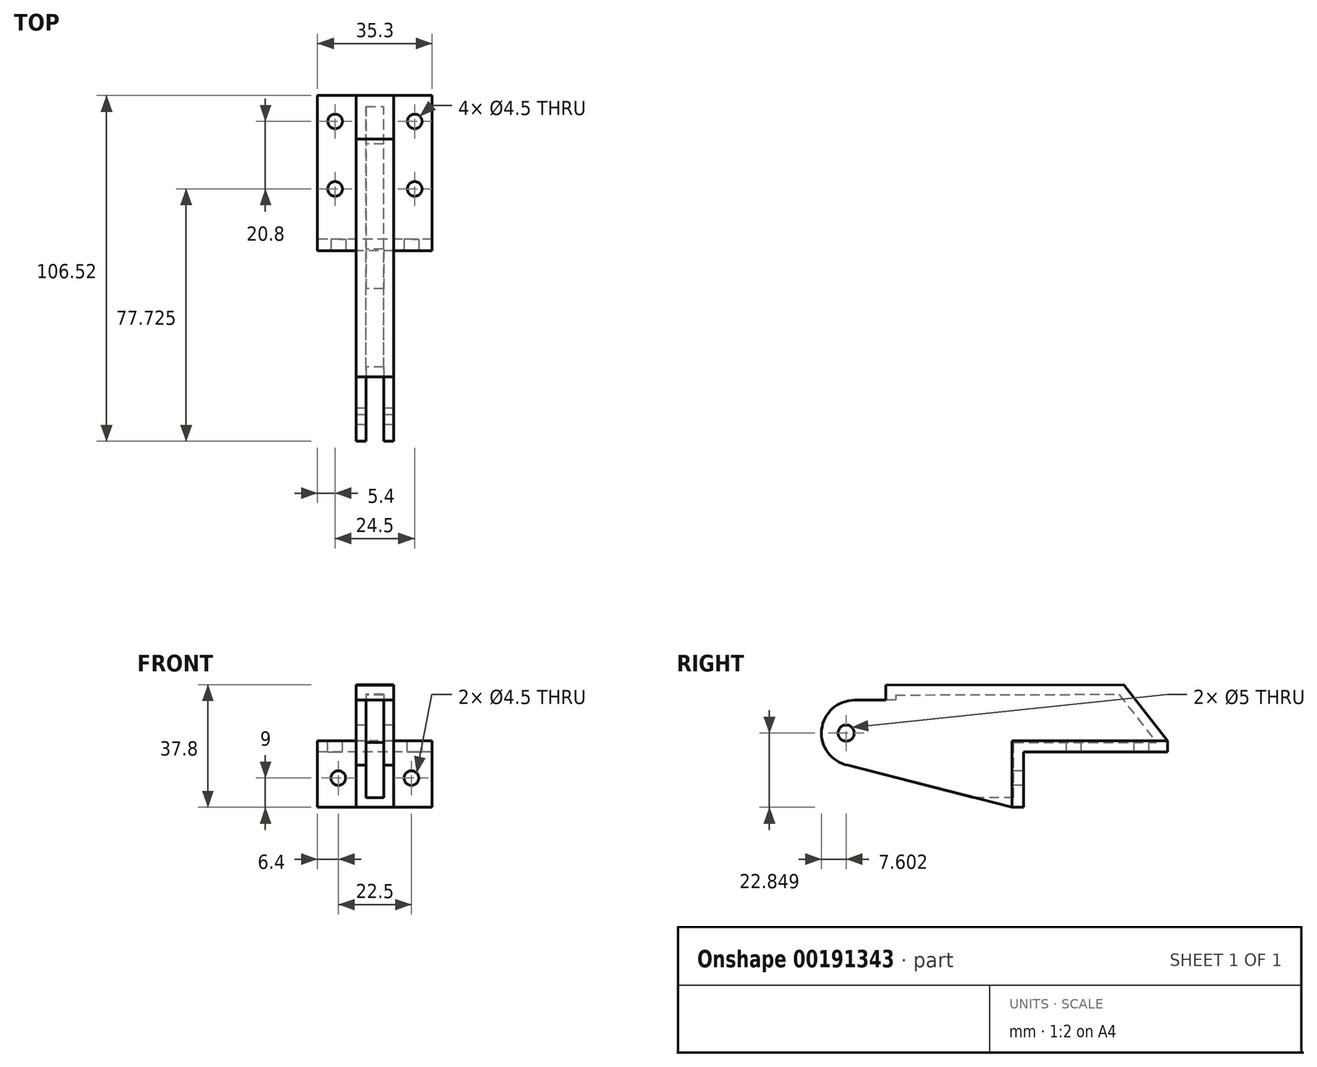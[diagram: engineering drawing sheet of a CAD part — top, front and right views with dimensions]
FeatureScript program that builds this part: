
annotation { "Feature Type Name" : "Feature", "Feature Type Description" : "" }
export const myFeature = defineFeature(function(context is Context, id is Id, definition is map)
    precondition{}
    {
        {
            var Q0;
            Q0=qCreatedBy(makeId("Right.planeOp"),FACE);
            var sketch = newSketch(context, id + "F0", { "sketchPlane" : qUnion([Q0])});
            skLineSegment(sketch, "E0", {"start": v(43.56, 12.13) * mm, "end": v(-0.74, 12.13) * mm});
            skLineSegment(sketch, "E1", {"start": v(-0.74, 12.13) * mm, "end": v(-0.74, -4.87) * mm});
            skLineSegment(sketch, "E2", {"start": v(-4.24, -4.87) * mm, "end": v(-4.24, 15.63) * mm});
            skLineSegment(sketch, "E3", {"start": v(-4.24, 15.63) * mm, "end": v(43.56, 15.63) * mm});
            skPoint(sketch, "E4", {"position": v(-43.14, 32.72) * mm});
            skLineSegment(sketch, "E5", {"start": v(-43.14, 32.72) * mm, "end": v(-43.14, 28.12) * mm});
            skLineSegment(sketch, "E6", {"start": v(-43.14, 32.72) * mm, "end": v(30.06, 32.93) * mm});
            skLineSegment(sketch, "E7", {"start": v(-4.24, -4.87) * mm, "end": v(-0.74, -4.87) * mm});
            skLineSegment(sketch, "E8", {"start": v(-43.14, 28.12) * mm, "end": v(-52.82, 28.12) * mm});
            skLineSegment(sketch, "E9", {"start": v(-54.83, 8.04) * mm, "end": v(-4.24, -4.87) * mm});
            skLineSegment(sketch, "E10", {"start": v(30.06, 32.93) * mm, "end": v(43.56, 15.63) * mm});
            skLineSegment(sketch, "E11", {"start": v(43.56, 12.13) * mm, "end": v(43.56, 15.63) * mm});
            skArc(sketch, "E12", {"start": v(-52.82, 28.12) * mm, "mid": v(-62.9, 18.99) * mm, "end": v(-54.83, 8.04) * mm});
            skCircle(sketch, "E13", {"center": v(-55.36, 17.98) * mm, "radius": 2.5 * mm});
            skLineSegment(sketch, "E14", {"start": v(-39.09, 32.73) * mm, "end": v(-39.02, 10.92) * mm});
            skLineSegment(sketch, "E15", {"start": v(-30.35, 32.75) * mm, "end": v(-30.28, 7.93) * mm});
            skLineSegment(sketch, "E16", {"start": v(-21.84, 32.78) * mm, "end": v(-21.77, 5.63) * mm});
            skLineSegment(sketch, "E17", {"start": v(-11.04, 32.81) * mm, "end": v(-10.95, 2.64) * mm});
            skLineSegment(sketch, "E18", {"start": v(1.6, 32.85) * mm, "end": v(1.65, 18.28) * mm});
            skLineSegment(sketch, "E19", {"start": v(12.87, 32.88) * mm, "end": v(12.92, 18.28) * mm});
            skLineSegment(sketch, "E20", {"start": v(24.83, 32.91) * mm, "end": v(24.87, 18.74) * mm});
            skLineSegment(sketch, "E21", {"start": v(35.03, 26.57) * mm, "end": v(35.03, 18.28) * mm});
            skSolve(sketch);
        }
        {
            var Q0;
            Q0=makeQuery(id+"F0.imprint","IMPRINT",FACE,{"disambiguationData":[TD([[makeQuery(id+"F0.imprint","IMPRINT",EDGE,{"derivedFrom":sQuery(id+"F0.wireOp",EDGE,"E2")}),1.0]])]});
            extrude(context, id + "F1", {"entities" : qUnion([Q0]), "endBound" : BoundingType.SYMMETRIC, "depth" : 11.5 * mm});
        }
        {
            var Q0;
            Q0=makeQuery(id+"F0.imprint","IMPRINT",FACE,{"disambiguationData":[TD([[makeQuery(id+"F0.imprint","IMPRINT",EDGE,{"derivedFrom":sQuery(id+"F0.wireOp",EDGE,"E0")}),-1.0]])]});
            extrude(context, id + "F2", {"entities" : qUnion([Q0]), "operationType" : NewBodyOperationType.ADD, "endBound" : BoundingType.SYMMETRIC, "depth" : 35.3 * mm});
        }
        {
            var Q0;
            Q0=makeQuery(id+"F1.opExtrude","SWEPT_FACE",FACE,{"disambiguationData":[OSD([sQuery(id+"F0.wireOp",EDGE,"E8")])]});
            var Q1;
            Q1=makeQuery(id+"F1.opExtrude","SWEPT_FACE",FACE,{"disambiguationData":[OSD([sQuery(id+"F0.wireOp",EDGE,"E9")])]});
            var Q2;
            Q2=makeQuery(id+"F1.opExtrude","SWEPT_FACE",FACE,{"disambiguationData":[OSD([sQuery(id+"F0.wireOp",EDGE,"E12")])]});
            var Q3;
            Q3=makeQuery(id+"F1.opExtrude","SWEPT_FACE",FACE,{"disambiguationData":[OSD([sQuery(id+"F0.wireOp",EDGE,"E13")])]});
            shell(context, id + "F3", {"entities" : qUnion([Q0, Q1, Q2, Q3]), "thickness" : 3 * mm});
        }
        {
            var Q0;
            {var subQ0=sQuery(id+"F0.wireOp",EDGE,"E3");var subQ1=sQuery(id+"F0.wireOp",EDGE,"E7");var subQ2=sQuery(id+"F0.wireOp",EDGE,"E2");Q0=makeQuery(id+"F2.boolean.opBoolean","SPLIT",FACE,{"disambiguationData":[TD([makeQuery(id+"F2.opExtrude","CAP_FACE",FACE,{"disambiguationData":[OSD([sQuery(id+"F0.wireOp",EDGE,"E0"),sQuery(id+"F0.wireOp",EDGE,"E1"),subQ2,subQ0,subQ1,sQuery(id+"F0.wireOp",EDGE,"E11")])],"isStart":false})])],"derivedFrom":makeQuery(id+"F2.opExtrude","SWEPT_FACE",FACE,{"disambiguationData":[OSD([subQ2])]})});}
            var sketch = newSketch(context, id + "F4", { "sketchPlane" : qUnion([Q0])});
            skPoint(sketch, "E22", {"position": v(11.25, 4.13) * mm});
            skPoint(sketch, "E23", {"position": v(-11.25, 4.13) * mm});
            skSolve(sketch);
        }
        {
            var Q0;
            Q0=sQuery(id+"F4.wireOp",VERTEX,"E22");
            var Q1;
            Q1=makeQuery(id+"F1.opExtrude","SWEPT_BODY",BODY,{"disambiguationData":[OSD([sQuery(id+"F0.wireOp",EDGE,"E2"),sQuery(id+"F0.wireOp",EDGE,"E3"),sQuery(id+"F0.wireOp",EDGE,"E5"),sQuery(id+"F0.wireOp",EDGE,"E6"),sQuery(id+"F0.wireOp",EDGE,"E8"),sQuery(id+"F0.wireOp",EDGE,"E9"),sQuery(id+"F0.wireOp",EDGE,"E10"),sQuery(id+"F0.wireOp",EDGE,"E12"),sQuery(id+"F0.wireOp",EDGE,"E13")])]});
            hole(context, id + "F5", {"style" : HoleStyle.SIMPLE, "endStyle" : HoleEndStyle.THROUGH, "holeDiameter" : 4.5 * mm, "locations" : qUnion([Q0]), "scope" : qUnion([Q1]), "isTappedThrough" : true});
        }
        {
            var Q0;
            {var subQ0=sQuery(id+"F0.wireOp",EDGE,"E2");var subQ1=sQuery(id+"F0.wireOp",EDGE,"E11");var subQ2=sQuery(id+"F0.wireOp",EDGE,"E3");Q0=makeQuery(id+"F2.boolean.opBoolean","SPLIT",FACE,{"disambiguationData":[TD([makeQuery(id+"F2.opExtrude","CAP_FACE",FACE,{"disambiguationData":[OSD([sQuery(id+"F0.wireOp",EDGE,"E0"),sQuery(id+"F0.wireOp",EDGE,"E1"),subQ0,subQ2,sQuery(id+"F0.wireOp",EDGE,"E7"),subQ1])],"isStart":false})])],"derivedFrom":makeQuery(id+"F2.opExtrude","SWEPT_FACE",FACE,{"disambiguationData":[OSD([subQ2])]})});}
            var sketch = newSketch(context, id + "F6", { "sketchPlane" : qUnion([Q0])});
            skPoint(sketch, "E24", {"position": v(12.25, 35.56) * mm});
            skPoint(sketch, "E25", {"position": v(12.25, 14.76) * mm});
            skPoint(sketch, "E26", {"position": v(-12.25, 14.76) * mm});
            skPoint(sketch, "E27", {"position": v(-12.25, 35.56) * mm});
            skSolve(sketch);
        }
        {
            var Q0;
            Q0=sQuery(id+"F6.wireOp",VERTEX,"E27");
            var Q1;
            Q1=sQuery(id+"F6.wireOp",VERTEX,"E26");
            var Q2;
            Q2=sQuery(id+"F6.wireOp",VERTEX,"E25");
            var Q3;
            Q3=sQuery(id+"F6.wireOp",VERTEX,"E24");
            var Q4;
            Q4=makeQuery(id+"F1.opExtrude","SWEPT_BODY",BODY,{"disambiguationData":[OSD([sQuery(id+"F0.wireOp",EDGE,"E2"),sQuery(id+"F0.wireOp",EDGE,"E3"),sQuery(id+"F0.wireOp",EDGE,"E5"),sQuery(id+"F0.wireOp",EDGE,"E6"),sQuery(id+"F0.wireOp",EDGE,"E8"),sQuery(id+"F0.wireOp",EDGE,"E9"),sQuery(id+"F0.wireOp",EDGE,"E10"),sQuery(id+"F0.wireOp",EDGE,"E12"),sQuery(id+"F0.wireOp",EDGE,"E13")])]});
            hole(context, id + "F7", {"style" : HoleStyle.SIMPLE, "endStyle" : HoleEndStyle.THROUGH, "holeDiameter" : 4.5 * mm, "locations" : qUnion([Q0, Q1, Q2, Q3]), "scope" : qUnion([Q4]), "isTappedThrough" : true});
        }
        {
            var Q0;
            Q0=sQuery(id+"F4.wireOp",VERTEX,"E23");
            var Q1;
            Q1=makeQuery(id+"F1.opExtrude","SWEPT_BODY",BODY,{"disambiguationData":[OSD([sQuery(id+"F0.wireOp",EDGE,"E2"),sQuery(id+"F0.wireOp",EDGE,"E3"),sQuery(id+"F0.wireOp",EDGE,"E5"),sQuery(id+"F0.wireOp",EDGE,"E6"),sQuery(id+"F0.wireOp",EDGE,"E8"),sQuery(id+"F0.wireOp",EDGE,"E9"),sQuery(id+"F0.wireOp",EDGE,"E10"),sQuery(id+"F0.wireOp",EDGE,"E12"),sQuery(id+"F0.wireOp",EDGE,"E13")])]});
            hole(context, id + "F8", {"style" : HoleStyle.SIMPLE, "endStyle" : HoleEndStyle.THROUGH, "holeDiameter" : 4.5 * mm, "locations" : qUnion([Q0]), "scope" : qUnion([Q1]), "isTappedThrough" : true});
        }
    });
